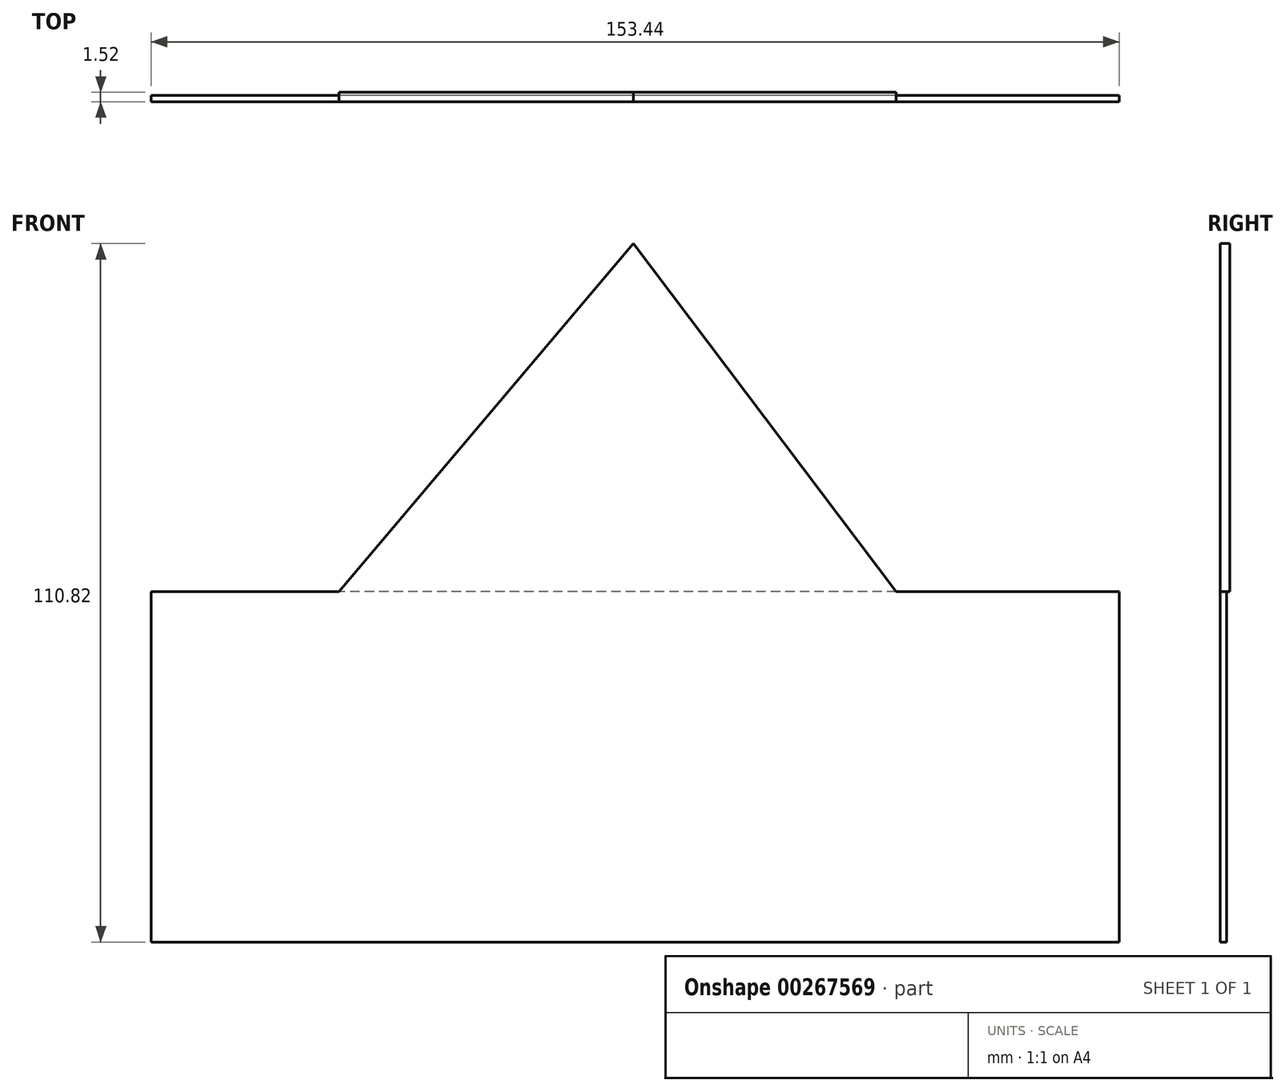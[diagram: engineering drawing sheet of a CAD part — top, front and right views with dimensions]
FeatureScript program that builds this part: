
annotation { "Feature Type Name" : "Feature", "Feature Type Description" : "" }
export const myFeature = defineFeature(function(context is Context, id is Id, definition is map)
    precondition{}
    {
        {
            var Q0;
            Q0=qCreatedBy(makeId("Front.planeOp"),FACE);
            var sketch = newSketch(context, id + "F0", { "sketchPlane" : qUnion([Q0])});
            skLineSegment(sketch, "E0", {"start": v(41.6, 0) * mm, "end": v(0, 55.8) * mm});
            skLineSegment(sketch, "E1", {"start": v(0, 55.8) * mm, "end": v(-42.3, 0) * mm});
            skLineSegment(sketch, "E2", {"start": v(-42.3, 0) * mm, "end": v(0, 0) * mm});
            skLineSegment(sketch, "E3", {"start": v(0, 0) * mm, "end": v(41.6, 0) * mm});
            skLineSegment(sketch, "E4", {"start": v(0, 0) * mm, "end": v(0, 55.8) * mm});
            skLineSegment(sketch, "E5", {"start": v(-26.28, 21.13) * mm, "end": v(25.85, 21.13) * mm});
            skLineSegment(sketch, "E6", {"start": v(-26.28, 21.13) * mm, "end": v(0, 0) * mm});
            skLineSegment(sketch, "E7", {"start": v(0, 0) * mm, "end": v(25.85, 21.13) * mm});
            skLineSegment(sketch, "E8", {"start": v(25.85, -42.18) * mm, "end": v(-26.28, -42.18) * mm});
            skLineSegment(sketch, "E9", {"start": v(-26.28, -42.18) * mm, "end": v(-26.28, 21.13) * mm});
            skLineSegment(sketch, "E10", {"start": v(25.85, 21.13) * mm, "end": v(25.85, -42.18) * mm});
            skLineSegment(sketch, "E11", {"start": v(0, -1.76) * mm, "end": v(0, -42.18) * mm});
            skLineSegment(sketch, "E12", {"start": v(0, -42.18) * mm, "end": v(-26.28, 0) * mm});
            skLineSegment(sketch, "E13", {"start": v(-26.28, 0) * mm, "end": v(0, -42.18) * mm});
            skLineSegment(sketch, "E14", {"start": v(0, -42.18) * mm, "end": v(25.85, 0) * mm});
            skLineSegment(sketch, "E15", {"start": v(41.6, 0) * mm, "end": v(41.6, -42.18) * mm});
            skLineSegment(sketch, "E16", {"start": v(-42.3, 0) * mm, "end": v(-42.3, -42.18) * mm});
            skLineSegment(sketch, "E17", {"start": v(-42.3, -42.18) * mm, "end": v(-26.28, -42.18) * mm});
            skLineSegment(sketch, "E18", {"start": v(25.85, -42.18) * mm, "end": v(41.6, -42.18) * mm});
            skCircle(sketch, "E19", {"center": v(0, 0) * mm, "radius": 13.25 * mm});
            skLineSegment(sketch, "E20", {"start": v(-42.3, -21.09) * mm, "end": v(-26.28, -21.09) * mm});
            skPoint(sketch, "E21.startSnap0", {"position": v(12.92, -21.09) * mm});
            skLineSegment(sketch, "E22", {"start": v(25.85, -21.09) * mm, "end": v(41.6, -21.09) * mm});
            skSolve(sketch);
        }
        {
            var Q0;
            {var subQ0=sQuery(id+"F0.wireOp",EDGE,"E4");var subQ3=sQuery(id+"F0.wireOp",EDGE,"E5");var subQ5=makeQuery(id+"F0.imprint","INTERSECT",VERTEX,{"derivedFrom":[subQ0,subQ3]});Q0=makeQuery(id+"F0.imprint","IMPRINT",FACE,{"disambiguationData":[TD([[makeQuery(id+"F0.imprint","IMPRINT",EDGE,{"disambiguationData":[TD([[subQ5,-1.0]])],"derivedFrom":subQ0}),-1.0]])]});}
            var Q1;
            Q1=sQuery(id+"F0.wireOp",EDGE,"E0");
            extrude(context, id + "F1", {"entities" : qUnion([Q0]), "bodyType" : ToolBodyType.SURFACE, "surfaceEntities" : qUnion([Q1]), "depth" : 25.4 * mm});
        }
        {
            var Q0;
            Q0=qCreatedBy(makeId("Front.planeOp"),FACE);
            var sketch = newSketch(context, id + "F2", { "sketchPlane" : qUnion([Q0])});
            skLineSegment(sketch, "E23", {"start": v(0, 55.97) * mm, "end": v(-46.63, 0) * mm});
            skSolve(sketch);
        }
        {
            var Q0;
            Q0=sQuery(id+"F2.wireOp",EDGE,"E23");
            extrude(context, id + "F3", {"bodyType" : ToolBodyType.SURFACE, "surfaceEntities" : qUnion([Q0]), "depth" : 25.4 * mm});
        }
        {
            var Q0;
            Q0=qCreatedBy(makeId("Front.planeOp"),FACE);
            var sketch = newSketch(context, id + "F4", { "sketchPlane" : qUnion([Q0])});
            skLineSegment(sketch, "E24", {"start": v(-46.3, 0) * mm, "end": v(42.53, 0) * mm});
            skSolve(sketch);
        }
        {
            var Q0;
            Q0=sQuery(id+"F4.wireOp",EDGE,"E24");
            extrude(context, id + "F5", {"bodyType" : ToolBodyType.SURFACE, "surfaceEntities" : qUnion([Q0]), "depth" : 25.4 * mm});
        }
        {
            var Q0;
            Q0=qCreatedBy(makeId("Front.planeOp"),FACE);
            var sketch = newSketch(context, id + "F6", { "sketchPlane" : qUnion([Q0])});
            skLineSegment(sketch, "E25", {"start": v(0, 54.63) * mm, "end": v(0, 0) * mm});
            skSolve(sketch);
        }
        {
            var Q0;
            Q0=sQuery(id+"F6.wireOp",EDGE,"E25");
            extrude(context, id + "F7", {"bodyType" : ToolBodyType.SURFACE, "surfaceEntities" : qUnion([Q0]), "depth" : 25.4 * mm});
        }
        {
            var Q0;
            Q0=qCreatedBy(makeId("Front.planeOp"),FACE);
            var sketch = newSketch(context, id + "F8", { "sketchPlane" : qUnion([Q0])});
            skLineSegment(sketch, "E26", {"start": v(-26.55, 23.62) * mm, "end": v(23.73, 23.62) * mm});
            skSolve(sketch);
        }
        {
            var Q0;
            Q0=sQuery(id+"F8.wireOp",EDGE,"E26");
            extrude(context, id + "F9", {"bodyType" : ToolBodyType.SURFACE, "surfaceEntities" : qUnion([Q0]), "depth" : 25.4 * mm});
        }
        {
            var Q0;
            Q0=qCreatedBy(makeId("Front.planeOp"),FACE);
            var sketch = newSketch(context, id + "F10", { "sketchPlane" : qUnion([Q0])});
            skLineSegment(sketch, "E27", {"start": v(-26.32, 23.15) * mm, "end": v(0, 0) * mm});
            skSolve(sketch);
        }
        {
            var Q0;
            Q0=sQuery(id+"F10.wireOp",EDGE,"E27");
            extrude(context, id + "F11", {"bodyType" : ToolBodyType.SURFACE, "surfaceEntities" : qUnion([Q0]), "depth" : 25.4 * mm});
        }
        {
            var Q0;
            Q0=qCreatedBy(makeId("Front.planeOp"),FACE);
            var sketch = newSketch(context, id + "F12", { "sketchPlane" : qUnion([Q0])});
            skLineSegment(sketch, "E28", {"start": v(0, 0) * mm, "end": v(23.73, 23.85) * mm});
            skSolve(sketch);
        }
        {
            var Q0;
            Q0=sQuery(id+"F12.wireOp",EDGE,"E28");
            extrude(context, id + "F13", {"bodyType" : ToolBodyType.SURFACE, "surfaceEntities" : qUnion([Q0]), "depth" : 25.4 * mm});
        }
        {
            var Q0;
            Q0=qCreatedBy(makeId("Front.planeOp"),FACE);
            var sketch = newSketch(context, id + "F14", { "sketchPlane" : qUnion([Q0])});
            skLineSegment(sketch, "E29", {"start": v(41.83, 0) * mm, "end": v(76.6, 0) * mm});
            skSolve(sketch);
        }
        {
            var Q0;
            Q0=sQuery(id+"F14.wireOp",EDGE,"E29");
            extrude(context, id + "F15", {"bodyType" : ToolBodyType.SURFACE, "surfaceEntities" : qUnion([Q0]), "depth" : 25.4 * mm});
        }
        {
            var Q0;
            Q0=qCreatedBy(makeId("Front.planeOp"),FACE);
            var sketch = newSketch(context, id + "F16", { "sketchPlane" : qUnion([Q0])});
            skLineSegment(sketch, "E30", {"start": v(-47.26, 0) * mm, "end": v(-47.26, -56.04) * mm});
            skSolve(sketch);
        }
        {
            var Q0;
            Q0=sQuery(id+"F16.wireOp",EDGE,"E30");
            extrude(context, id + "F17", {"bodyType" : ToolBodyType.SURFACE, "surfaceEntities" : qUnion([Q0]), "depth" : 25.4 * mm});
        }
        {
            var Q0;
            Q0=qCreatedBy(makeId("Front.planeOp"),FACE);
            var sketch = newSketch(context, id + "F18", { "sketchPlane" : qUnion([Q0])});
            skLineSegment(sketch, "E31", {"start": v(-76.85, -55.57) * mm, "end": v(75.88, -55.57) * mm});
            skSolve(sketch);
        }
        {
            var Q0;
            Q0=sQuery(id+"F18.wireOp",EDGE,"E31");
            extrude(context, id + "F19", {"bodyType" : ToolBodyType.SURFACE, "surfaceEntities" : qUnion([Q0]), "depth" : 25.4 * mm});
        }
        {
            var Q0;
            Q0=qCreatedBy(makeId("Front.planeOp"),FACE);
            var sketch = newSketch(context, id + "F20", { "sketchPlane" : qUnion([Q0])});
            skLineSegment(sketch, "E32", {"start": v(0, 0) * mm, "end": v(0, -54.63) * mm});
            skSolve(sketch);
        }
        {
            var Q0;
            Q0=sQuery(id+"F20.wireOp",EDGE,"E32");
            extrude(context, id + "F21", {"bodyType" : ToolBodyType.SURFACE, "surfaceEntities" : qUnion([Q0]), "depth" : 25.4 * mm});
        }
        {
            var Q0;
            Q0=qCreatedBy(makeId("Front.planeOp"),FACE);
            var sketch = newSketch(context, id + "F22", { "sketchPlane" : qUnion([Q0])});
            skLineSegment(sketch, "E33", {"start": v(41.47, 0) * mm, "end": v(41.47, -55.34) * mm});
            skSolve(sketch);
        }
        {
            var Q0;
            Q0=sQuery(id+"F22.wireOp",EDGE,"E33");
            extrude(context, id + "F23", {"bodyType" : ToolBodyType.SURFACE, "surfaceEntities" : qUnion([Q0]), "depth" : 25.4 * mm});
        }
        {
            var Q0;
            Q0=qCreatedBy(makeId("Front.planeOp"),FACE);
            var sketch = newSketch(context, id + "F24", { "sketchPlane" : qUnion([Q0])});
            skLineSegment(sketch, "E34", {"start": v(76.24, 0) * mm, "end": v(76.24, -56.04) * mm});
            skSolve(sketch);
        }
        {
            var Q0;
            Q0=sQuery(id+"F24.wireOp",EDGE,"E34");
            extrude(context, id + "F25", {"bodyType" : ToolBodyType.SURFACE, "surfaceEntities" : qUnion([Q0]), "depth" : 25.4 * mm});
        }
        {
            var Q0;
            Q0=qCreatedBy(makeId("Front.planeOp"),FACE);
            var sketch = newSketch(context, id + "F26", { "sketchPlane" : qUnion([Q0])});
            skLineSegment(sketch, "E35", {"start": v(-76.26, -18.45) * mm, "end": v(76, -18.45) * mm});
            skSolve(sketch);
        }
        {
            var Q0;
            Q0=sQuery(id+"F26.wireOp",EDGE,"E35");
            extrude(context, id + "F27", {"bodyType" : ToolBodyType.SURFACE, "surfaceEntities" : qUnion([Q0]), "depth" : 25.4 * mm});
        }
        {
            var Q0;
            Q0=qCreatedBy(makeId("Front.planeOp"),FACE);
            var sketch = newSketch(context, id + "F28", { "sketchPlane" : qUnion([Q0])});
            skLineSegment(sketch, "E36", {"start": v(-76.26, 0) * mm, "end": v(-76.26, -55.1) * mm});
            skSolve(sketch);
        }
        {
            var Q0;
            Q0=sQuery(id+"F28.wireOp",EDGE,"E36");
            extrude(context, id + "F29", {"bodyType" : ToolBodyType.SURFACE, "surfaceEntities" : qUnion([Q0]), "depth" : 25.4 * mm});
        }
        {
            var Q0;
            Q0=qCreatedBy(makeId("Front.planeOp"),FACE);
            var sketch = newSketch(context, id + "F30", { "sketchPlane" : qUnion([Q0])});
            skLineSegment(sketch, "E37", {"start": v(-75.79, 0) * mm, "end": v(-47.12, 0) * mm});
            skSolve(sketch);
        }
        {
            var Q0;
            Q0=sQuery(id+"F30.wireOp",EDGE,"E37");
            extrude(context, id + "F31", {"bodyType" : ToolBodyType.SURFACE, "surfaceEntities" : qUnion([Q0]), "depth" : 25.4 * mm});
        }
        {
            var Q0;
            Q0=qCreatedBy(makeId("Front.planeOp"),FACE);
            var sketch = newSketch(context, id + "F32", { "sketchPlane" : qUnion([Q0])});
            skLineSegment(sketch, "E38", {"start": v(-76.26, -41.7) * mm, "end": v(76.71, -41.7) * mm});
            skSolve(sketch);
        }
        {
            var Q0;
            Q0=sQuery(id+"F32.wireOp",EDGE,"E38");
            extrude(context, id + "F33", {"bodyType" : ToolBodyType.SURFACE, "surfaceEntities" : qUnion([Q0]), "depth" : 25.4 * mm});
        }
        {
            var Q0;
            Q0=qCreatedBy(makeId("Front.planeOp"),FACE);
            var sketch = newSketch(context, id + "F34", { "sketchPlane" : qUnion([Q0])});
            skLineSegment(sketch, "E39.bottom", {"start": v(77, 0) * mm, "end": v(-76.44, 0) * mm});
            skLineSegment(sketch, "E39.top", {"start": v(77, -55.57) * mm, "end": v(-76.44, -55.57) * mm});
            skLineSegment(sketch, "E39.left", {"start": v(77, 0) * mm, "end": v(77, -55.57) * mm});
            skLineSegment(sketch, "E39.right", {"start": v(-76.44, 0) * mm, "end": v(-76.44, -55.57) * mm});
            skSolve(sketch);
        }
        {
            var Q0;
            Q0=makeQuery(id+"F34.imprint","IMPRINT",FACE,{"disambiguationData":[TD([[makeQuery(id+"F34.imprint","IMPRINT",EDGE,{"derivedFrom":sQuery(id+"F34.wireOp",EDGE,"E39.bottom")}),1.0]])]});
            var Q1;
            Q1=sQuery(id+"F34.wireOp",EDGE,"E39.left");
            var Q2;
            Q2=sQuery(id+"F34.wireOp",EDGE,"E39.bottom");
            var Q3;
            Q3=sQuery(id+"F34.wireOp",EDGE,"E39.right");
            var Q4;
            Q4=sQuery(id+"F34.wireOp",EDGE,"E39.top");
            extrude(context, id + "F35", {"entities" : qUnion([Q0]), "surfaceEntities" : qUnion([Q1, Q2, Q3, Q4]), "oppositeDirection" : true, "depth" : 0.76 * mm});
        }
        {
            var Q0;
            Q0=qCreatedBy(makeId("Front.planeOp"),FACE);
            var sketch = newSketch(context, id + "F36", { "sketchPlane" : qUnion([Q0])});
            skLineSegment(sketch, "E40", {"start": v(0, 55.25) * mm, "end": v(41.68, 0) * mm});
            skLineSegment(sketch, "E41", {"start": v(41.68, 0) * mm, "end": v(-46.66, 0) * mm});
            skLineSegment(sketch, "E42", {"start": v(-46.66, 0) * mm, "end": v(0, 55.25) * mm});
            skSolve(sketch);
        }
        {
            var Q0;
            Q0=makeQuery(id+"F36.imprint","IMPRINT",FACE,{"disambiguationData":[TD([[makeQuery(id+"F36.imprint","IMPRINT",EDGE,{"derivedFrom":sQuery(id+"F36.wireOp",EDGE,"E40")}),-1.0]])]});
            var Q1;
            Q1=sQuery(id+"F36.wireOp",EDGE,"E42");
            extrude(context, id + "F37", {"entities" : qUnion([Q0]), "operationType" : NewBodyOperationType.ADD, "surfaceEntities" : qUnion([Q1]), "oppositeDirection" : true, "depth" : 1.27 * mm});
        }
        {
            var Q0;
            Q0=makeQuery(id+"F37.opExtrude","CAP_FACE",FACE,{"disambiguationData":[OSD([sQuery(id+"F36.wireOp",EDGE,"E40"),sQuery(id+"F36.wireOp",EDGE,"E41"),sQuery(id+"F36.wireOp",EDGE,"E42")])],"isStart":false});
            var sketch = newSketch(context, id + "F38", { "sketchPlane" : qUnion([Q0])});
            skSolve(sketch);
        }
        {
            var Q0;
            Q0=makeQuery(id+"F38.imprint","IMPRINT",FACE,{"disambiguationData":[TD([[makeQuery(id+"F38.imprint","IMPRINT",EDGE,{"derivedFrom":makeQuery(id+"F37.opExtrude","CAP_EDGE",EDGE,{"disambiguationData":[OSD([sQuery(id+"F36.wireOp",EDGE,"E40")])],"isStart":false})}),1.0]])]});
            extrude(context, id + "F39", {"entities" : qUnion([Q0]), "operationType" : NewBodyOperationType.ADD, "depth" : 0.25 * mm});
        }
        {
            var Q0;
            Q0=makeQuery(id+"F35.opExtrude","CAP_FACE",FACE,{"disambiguationData":[OSD([sQuery(id+"F34.wireOp",EDGE,"E39.bottom"),sQuery(id+"F34.wireOp",EDGE,"E39.top"),sQuery(id+"F34.wireOp",EDGE,"E39.left"),sQuery(id+"F34.wireOp",EDGE,"E39.right")])],"isStart":false});
            extrude(context, id + "F40", {"entities" : qUnion([Q0]), "operationType" : NewBodyOperationType.ADD, "depth" : 0.25 * mm});
        }
    });
